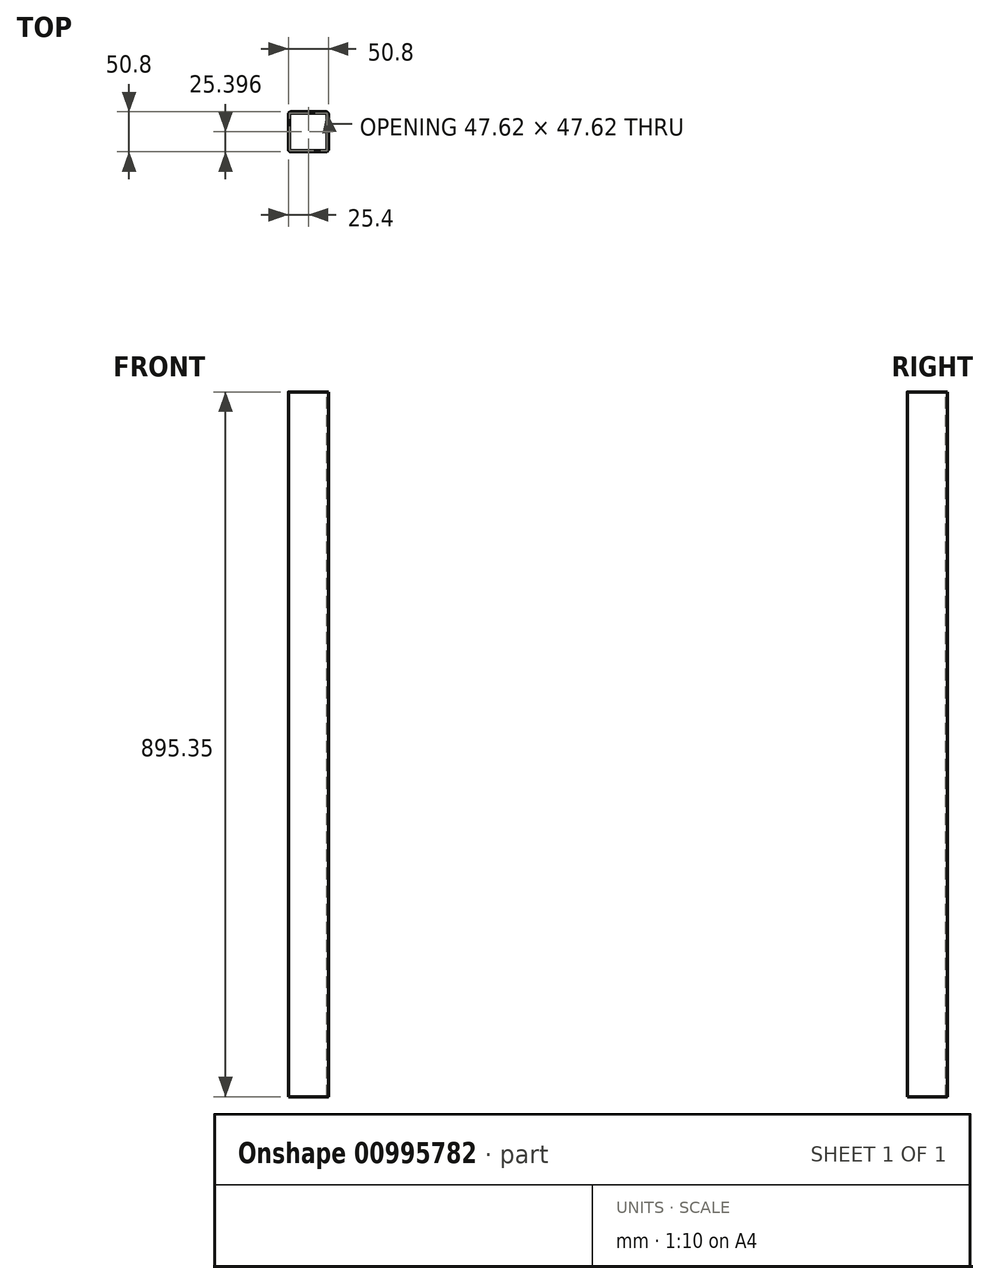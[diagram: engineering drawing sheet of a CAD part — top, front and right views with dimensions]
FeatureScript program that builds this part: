
annotation { "Feature Type Name" : "Feature", "Feature Type Description" : "" }
export const myFeature = defineFeature(function(context is Context, id is Id, definition is map)
    precondition{}
    {
        {
            var Q0;
            Q0=qCreatedBy(makeId("Top.planeOp"),FACE);
            var sketch = newSketch(context, id + "F0", { "sketchPlane" : qUnion([Q0])});
            skLineSegment(sketch, "E0.bottom", {"start": v(-38.1, -36.66) * mm, "end": v(12.7, -36.66) * mm});
            skLineSegment(sketch, "E0.top", {"start": v(-38.1, 14.14) * mm, "end": v(12.7, 14.14) * mm});
            skLineSegment(sketch, "E0.left", {"start": v(-38.1, -36.66) * mm, "end": v(-38.1, 14.14) * mm});
            skLineSegment(sketch, "E0.right", {"start": v(12.7, -36.66) * mm, "end": v(12.7, 14.14) * mm});
            skLineSegment(sketch, "E1.0", {"start": v(-36.51, -35.08) * mm, "end": v(-36.51, 12.55) * mm});
            skLineSegment(sketch, "E1.1", {"start": v(-36.51, -35.08) * mm, "end": v(11.11, -35.08) * mm});
            skLineSegment(sketch, "E1.2", {"start": v(11.11, -35.08) * mm, "end": v(11.11, 12.55) * mm});
            skLineSegment(sketch, "E1.3", {"start": v(-36.51, 12.55) * mm, "end": v(11.11, 12.55) * mm});
            skSolve(sketch);
        }
        {
            var Q0;
            Q0=makeQuery(id+"F0.imprint","IMPRINT",FACE,{"disambiguationData":[TD([[makeQuery(id+"F0.imprint","IMPRINT",EDGE,{"derivedFrom":sQuery(id+"F0.wireOp",EDGE,"E0.bottom")}),1.0]])]});
            extrude(context, id + "F1", {"entities" : qUnion([Q0]), "oppositeDirection" : true, "depth" : 895.35 * mm, "offsetDistance" : 25.4 * mm});
        }
        {
            var Q0;
            Q0=makeQuery(id+"F1.opExtrude","SWEPT_EDGE",EDGE,{"disambiguationData":[OSD([sQuery(id+"F0.wireOp",EDGE,"E0.bottom"),sQuery(id+"F0.wireOp",EDGE,"E0.left")])]});
            var Q1;
            Q1=makeQuery(id+"F1.opExtrude","SWEPT_EDGE",EDGE,{"disambiguationData":[OSD([sQuery(id+"F0.wireOp",EDGE,"E0.bottom"),sQuery(id+"F0.wireOp",EDGE,"E0.right")])]});
            var Q2;
            Q2=makeQuery(id+"F1.opExtrude","SWEPT_EDGE",EDGE,{"disambiguationData":[OSD([sQuery(id+"F0.wireOp",EDGE,"E0.top"),sQuery(id+"F0.wireOp",EDGE,"E0.right")])]});
            var Q3;
            Q3=makeQuery(id+"F1.opExtrude","SWEPT_EDGE",EDGE,{"disambiguationData":[OSD([sQuery(id+"F0.wireOp",EDGE,"E0.top"),sQuery(id+"F0.wireOp",EDGE,"E0.left")])]});
            fillet(context, id + "F2", {"entities" : qUnion([Q0, Q1, Q2, Q3]), "radius" : 3.17 * mm, "tangentPropagation" : true, "defaultsChanged" : true, "vertexSettings" : [], "allowEdgeOverflow" : false});
        }
        {
            var Q0;
            Q0=makeQuery(id+"F1.opExtrude","SWEPT_EDGE",EDGE,{"disambiguationData":[OSD([sQuery(id+"F0.wireOp",EDGE,"E1.0"),sQuery(id+"F0.wireOp",EDGE,"E1.3")])]});
            var Q1;
            Q1=makeQuery(id+"F1.opExtrude","SWEPT_EDGE",EDGE,{"disambiguationData":[OSD([sQuery(id+"F0.wireOp",EDGE,"E1.2"),sQuery(id+"F0.wireOp",EDGE,"E1.3")])]});
            var Q2;
            Q2=makeQuery(id+"F1.opExtrude","SWEPT_EDGE",EDGE,{"disambiguationData":[OSD([sQuery(id+"F0.wireOp",EDGE,"E1.1"),sQuery(id+"F0.wireOp",EDGE,"E1.2")])]});
            var Q3;
            Q3=makeQuery(id+"F1.opExtrude","SWEPT_EDGE",EDGE,{"disambiguationData":[OSD([sQuery(id+"F0.wireOp",EDGE,"E1.0"),sQuery(id+"F0.wireOp",EDGE,"E1.1")])]});
            fillet(context, id + "F3", {"entities" : qUnion([Q0, Q1, Q2, Q3]), "radius" : 1.59 * mm, "tangentPropagation" : true, "defaultsChanged" : true, "vertexSettings" : [], "allowEdgeOverflow" : false});
        }
    });
